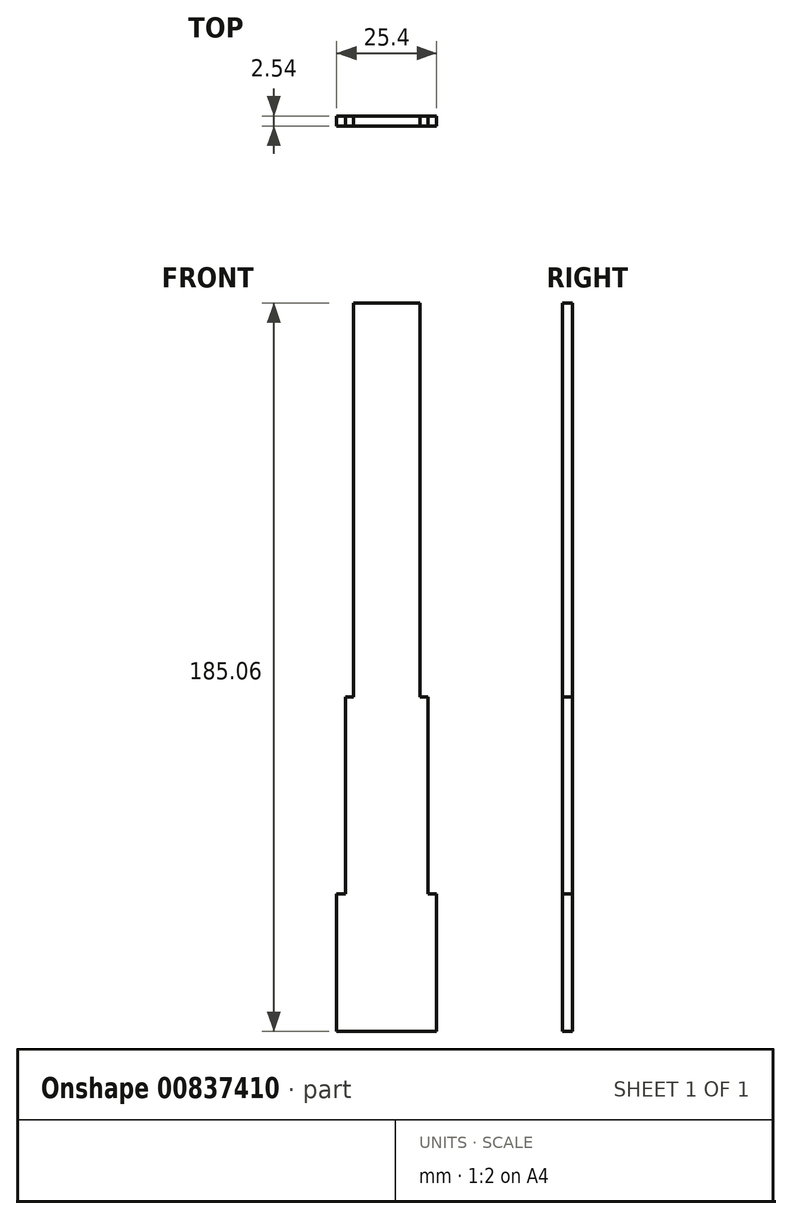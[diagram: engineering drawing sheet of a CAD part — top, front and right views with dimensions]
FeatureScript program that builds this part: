
annotation { "Feature Type Name" : "Feature", "Feature Type Description" : "" }
export const myFeature = defineFeature(function(context is Context, id is Id, definition is map)
    precondition{}
    {
        {
            var Q0;
            Q0=qCreatedBy(makeId("Front.planeOp"),FACE);
            var sketch = newSketch(context, id + "F0", { "sketchPlane" : qUnion([Q0])});
            skLineSegment(sketch, "E0", {"start": v(0, 0) * mm, "end": v(-12.7, 0) * mm});
            skLineSegment(sketch, "E1.MirrorCS", {"start": v(0, 0) * mm, "end": v(12.7, 0) * mm});
            skLineSegment(sketch, "E2", {"start": v(-12.7, 0) * mm, "end": v(-12.7, 34.98) * mm});
            skLineSegment(sketch, "E3", {"start": v(-12.7, 34.98) * mm, "end": v(12.7, 34.98) * mm});
            skLineSegment(sketch, "E4", {"start": v(12.7, 34.98) * mm, "end": v(12.7, 0) * mm});
            skLineSegment(sketch, "E5", {"start": v(-10.47, 34.98) * mm, "end": v(-10.47, 85.01) * mm});
            skLineSegment(sketch, "E6", {"start": v(10.47, 34.98) * mm, "end": v(10.47, 85.01) * mm});
            skLineSegment(sketch, "E7", {"start": v(10.47, 85.01) * mm, "end": v(-10.47, 85.01) * mm});
            skLineSegment(sketch, "E8", {"start": v(-8.47, 85.01) * mm, "end": v(-8.47, 185.06) * mm});
            skLineSegment(sketch, "E9", {"start": v(8.47, 85.01) * mm, "end": v(8.47, 185.06) * mm});
            skLineSegment(sketch, "E10", {"start": v(8.47, 185.06) * mm, "end": v(-8.47, 185.06) * mm});
            skSolve(sketch);
        }
        {
            var Q0;
            Q0=makeQuery(id+"F0.imprint","IMPRINT",FACE,{"disambiguationData":[TD([[makeQuery(id+"F0.imprint","IMPRINT",EDGE,{"derivedFrom":sQuery(id+"F0.wireOp",EDGE,"E0")}),-1.0]])]});
            var Q1;
            {var subQ1=sQuery(id+"F0.wireOp",EDGE,"E5");Q1=makeQuery(id+"F0.imprint","IMPRINT",FACE,{"disambiguationData":[TD([[makeQuery(id+"F0.imprint","IMPRINT",EDGE,{"derivedFrom":subQ1}),-1.0]])]});}
            var Q2;
            {var subQ0=sQuery(id+"F0.wireOp",EDGE,"E8");Q2=makeQuery(id+"F0.imprint","IMPRINT",FACE,{"disambiguationData":[TD([[makeQuery(id+"F0.imprint","IMPRINT",EDGE,{"derivedFrom":subQ0}),-1.0]])]});}
            extrude(context, id + "F1", {"entities" : qUnion([Q0, Q1, Q2]), "oppositeDirection" : true, "depth" : 2.54 * mm, "offsetDistance" : 25.4 * mm});
        }
    });
